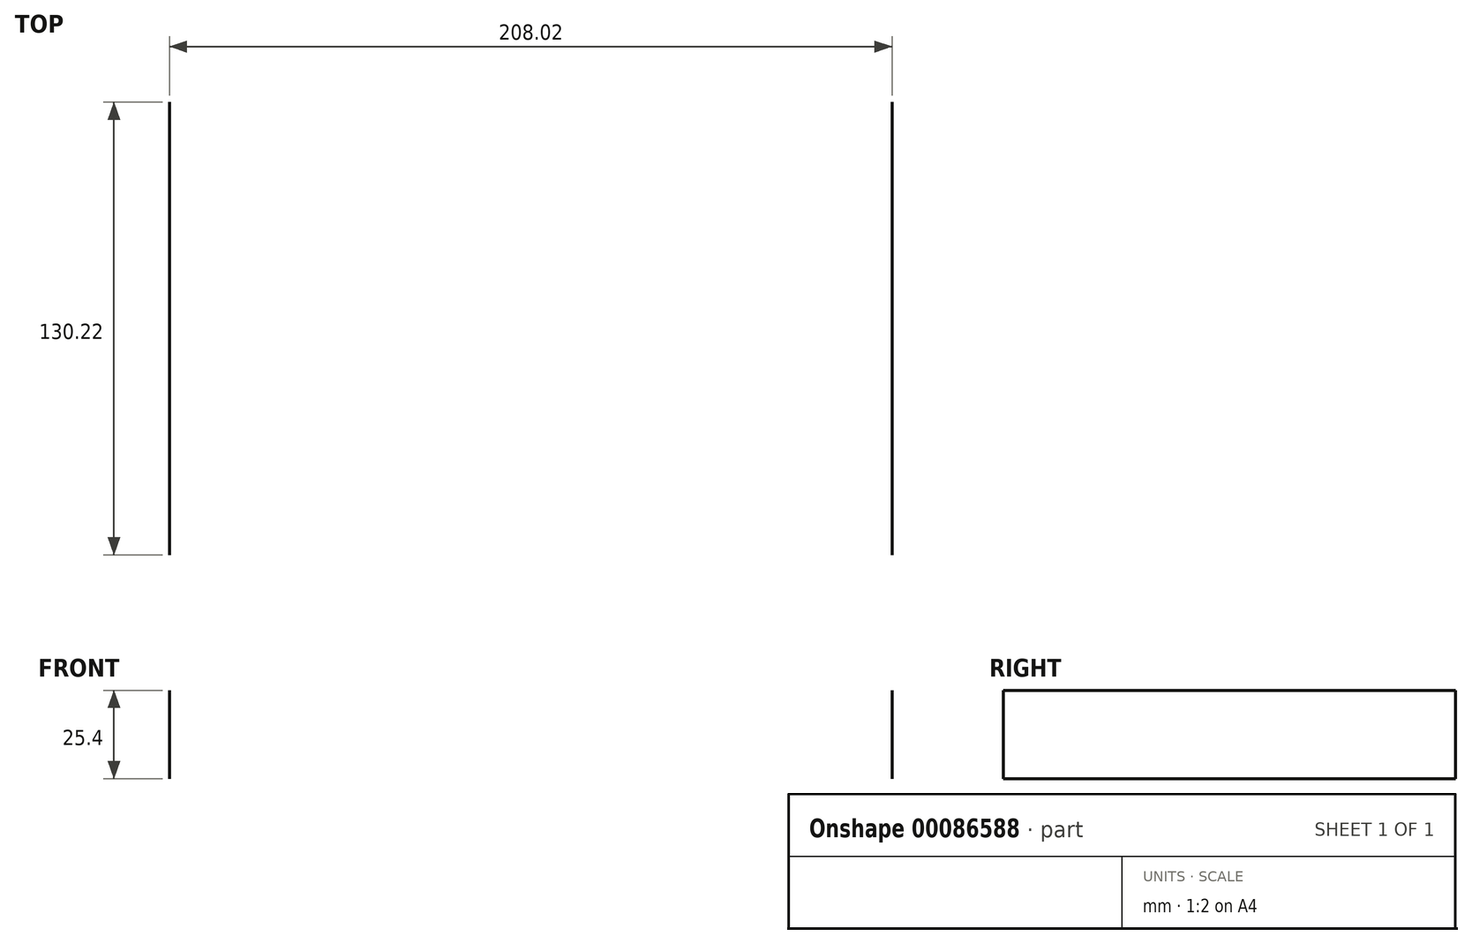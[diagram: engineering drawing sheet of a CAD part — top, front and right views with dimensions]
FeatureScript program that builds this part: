
annotation { "Feature Type Name" : "Feature", "Feature Type Description" : "" }
export const myFeature = defineFeature(function(context is Context, id is Id, definition is map)
    precondition{}
    {
        {
            var Q0;
            Q0=qCreatedBy(makeId("Top.planeOp"),FACE);
            var sketch = newSketch(context, id + "F0", { "sketchPlane" : qUnion([Q0])});
            skLineSegment(sketch, "E0.bottom", {"start": v(104, 65.1) * mm, "end": v(-104, 65.1) * mm});
            skLineSegment(sketch, "E0.top", {"start": v(104, -65.1) * mm, "end": v(-104, -65.1) * mm});
            skLineSegment(sketch, "E0.left", {"start": v(104, 65.1) * mm, "end": v(104, -65.1) * mm});
            skLineSegment(sketch, "E0.right", {"start": v(-104, 65.1) * mm, "end": v(-104, -65.1) * mm});
            skPoint(sketch, "E0.middle", {"position": v(0, 0) * mm});
            skSolve(sketch);
        }
        {
            var Q0;
            Q0=sQuery(id+"F0.wireOp",EDGE,"E0.right");
            var Q1;
            Q1=sQuery(id+"F0.wireOp",EDGE,"E0.left");
            extrude(context, id + "F1", {"bodyType" : ToolBodyType.SURFACE, "surfaceEntities" : qUnion([Q0, Q1]), "depth" : 25.4 * mm});
        }
    });
